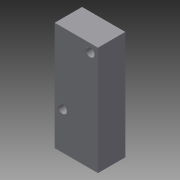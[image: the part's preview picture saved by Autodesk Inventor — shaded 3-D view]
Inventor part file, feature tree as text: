
AUTODESK INVENTOR PART (.ipt)
format: ipt  version: 2013 (Build 170138000, 138)  size: 87,040 bytes
history: native  units: in
note: dims shown in document units (in); Inventor stores cm internally (conversion verified against a paired STEP export)
features: extrude x2, sketch x2
ambient origin geometry x8: Origin, YZ Plane, XZ Plane, XY Plane, X Axis, Y Axis, Z Axis, Center Point
bodies: Solid1 (feature_tree)
feature tree (4):
  extrude  "Extrusion1"  Depth=0.623in
  extrude  "Extrusion2"  Depth=0.225in
  sketch  "Sketch1"  dims[d0=1.131in d1=0.623in]
  sketch  "Sketch2"  dims[d2=0.125in d3=0.225in d4=0.125in d5=0.225in d6=0.394in d7=0.0in d8=0.433in d9=0.394in d10=0.0in]
